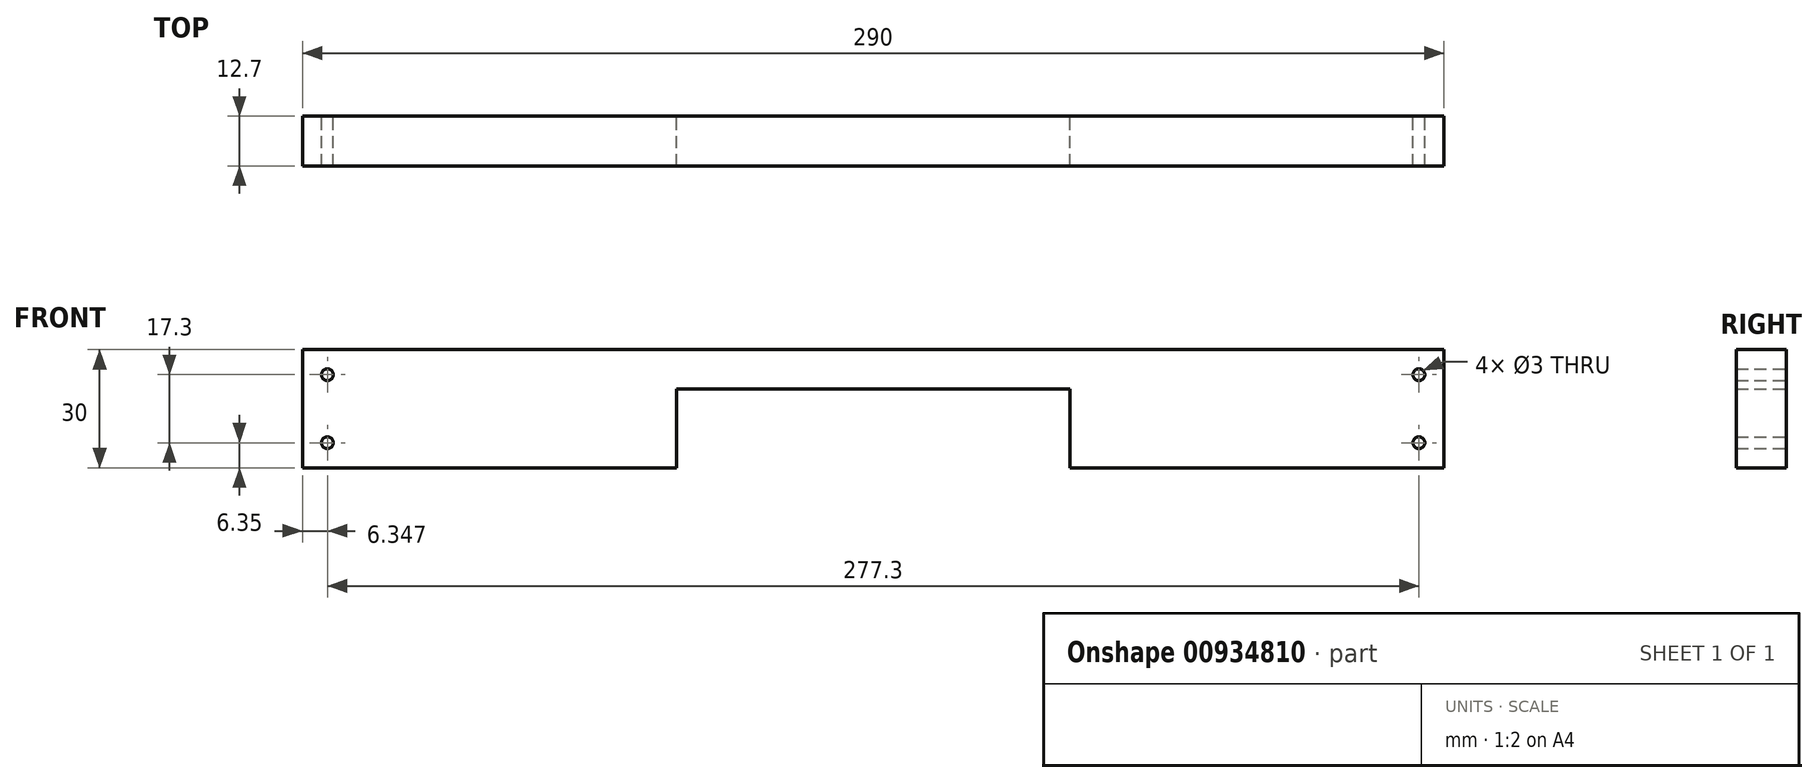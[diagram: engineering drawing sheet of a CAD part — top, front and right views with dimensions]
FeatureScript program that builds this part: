
annotation { "Feature Type Name" : "Feature", "Feature Type Description" : "" }
export const myFeature = defineFeature(function(context is Context, id is Id, definition is map)
    precondition{}
    {
        {
            var Q0;
            Q0=qCreatedBy(makeId("Front.planeOp"),FACE);
            var sketch = newSketch(context, id + "F0", { "sketchPlane" : qUnion([Q0])});
            skLineSegment(sketch, "E0.bottom", {"start": v(-140.73, -1.71) * mm, "end": v(149.27, -1.71) * mm});
            skLineSegment(sketch, "E0.top", {"start": v(-140.73, -31.71) * mm, "end": v(-45.73, -31.71) * mm});
            skLineSegment(sketch, "E0.left", {"start": v(-140.73, -1.71) * mm, "end": v(-140.73, -31.71) * mm});
            skLineSegment(sketch, "E0.right", {"start": v(149.27, -1.71) * mm, "end": v(149.27, -31.71) * mm});
            skLineSegment(sketch, "E1", {"start": v(-45.73, -31.71) * mm, "end": v(-45.73, -11.71) * mm});
            skLineSegment(sketch, "E2", {"start": v(-45.73, -11.71) * mm, "end": v(54.27, -11.71) * mm});
            skLineSegment(sketch, "E3", {"start": v(54.27, -11.71) * mm, "end": v(54.27, -31.71) * mm});
            skLineSegment(sketch, "E4.trimOffspring", {"start": v(54.27, -31.71) * mm, "end": v(149.27, -31.71) * mm});
            skLineSegment(sketch, "E5", {"start": v(-134.38, -1.71) * mm, "end": v(-134.38, -31.71) * mm, "construction": true});
            skLineSegment(sketch, "E6", {"start": v(4.27, -11.71) * mm, "end": v(4.27, 0) * mm, "construction": true});
            skCircle(sketch, "E7", {"center": v(-134.38, -8.06) * mm, "radius": 1.5 * mm});
            skLineSegment(sketch, "E8", {"start": v(-140.73, -16.71) * mm, "end": v(-45.73, -16.71) * mm, "construction": true});
            skCircle(sketch, "E9.MirrorC", {"center": v(-134.38, -25.36) * mm, "radius": 1.5 * mm});
            skCircle(sketch, "E10.MirrorC", {"center": v(142.92, -8.06) * mm, "radius": 1.5 * mm});
            skCircle(sketch, "E11.MirrorC", {"center": v(142.92, -25.36) * mm, "radius": 1.5 * mm});
            skSolve(sketch);
        }
        {
            var Q0;
            Q0 = qSketchRegion(id + "F0", true);
            extrude(context, id + "F1", {"entities" : qUnion([Q0]), "depth" : 12.7 * mm, "offsetDistance" : 25 * mm});
        }
    });
